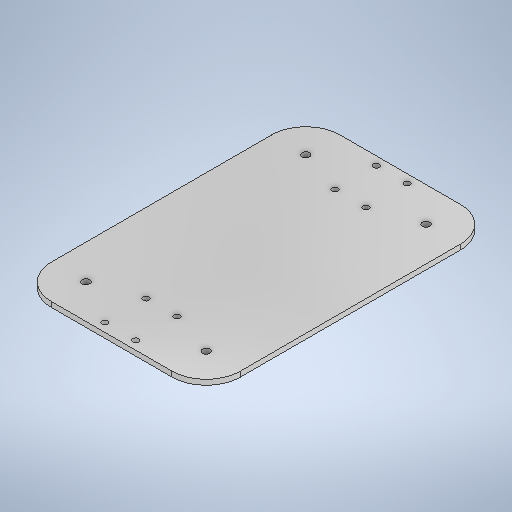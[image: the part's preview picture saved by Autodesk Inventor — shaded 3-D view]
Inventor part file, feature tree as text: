
AUTODESK INVENTOR PART (.ipt)
format: ipt  version: 2025.2 (Build 292293000, 293)  size: 284,160 bytes
history: native  units: mm
features: sketch x2, hole x2, plane x2, extrude x1, fillet x1
ambient origin geometry x8: Origin, YZ Plane, XZ Plane, XY Plane, X Axis, Y Axis, Z Axis, Center Point
bodies: Solid1 (feature_tree)
feature tree (8):
  sketch  "Sketch1"  dims[d4=110.0mm d5=168.0mm]
  extrude  "Extrusion2"  Depth=168.0mm
  hole  "Hole1"  [1 undecoded]
  fillet  "Fillet1"  Radius=18.0mm
  plane  "Work Plane1"
  plane  "Work Plane2"
  hole  "Hole2"  [1 undecoded]
  sketch  "Sketch2"  dims[d20=3.0mm d21=0.0mm d22=5.0mm d23=18.0mm d24=24.0mm d25=5.0mm d26=18.0mm d27=24.0mm d28=3.4mm d29=6.0mm d30=4.0mm d31=2.0mm d32=90.0deg d33=8.0mm d34=20.594885mm d35=20.0mm d36=-84.0mm d37=-55.0mm d38=4.3mm d39=6.0mm d40=4.0mm d41=2.0mm d42=90.0deg d43=8.0mm d44=20.594885mm]
note: 2 required parameter values undecoded (feature->parameter linkage not recoverable at this tier; creation-order binding heuristic only, values carry confidence <= 0.55)
